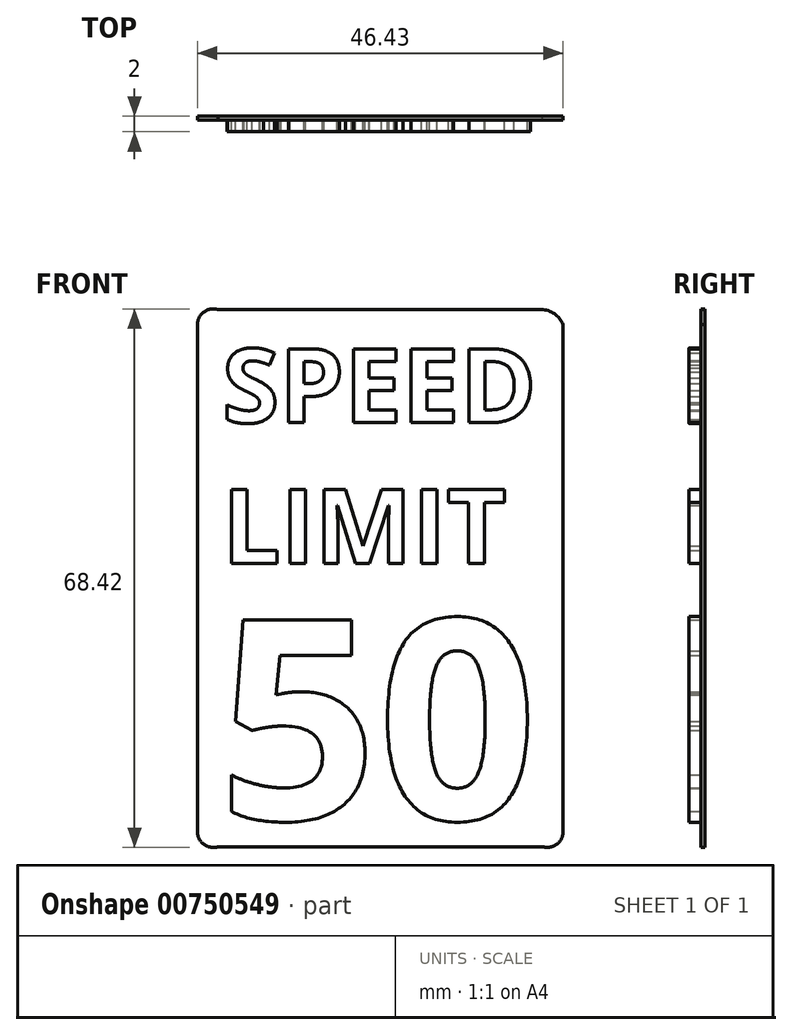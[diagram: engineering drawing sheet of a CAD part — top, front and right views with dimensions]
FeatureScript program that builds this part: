
annotation { "Feature Type Name" : "Feature", "Feature Type Description" : "" }
export const myFeature = defineFeature(function(context is Context, id is Id, definition is map)
    precondition{}
    {
        {
            var Q0;
            Q0=qCreatedBy(makeId("Front.planeOp"),FACE);
            var sketch = newSketch(context, id + "F0", { "sketchPlane" : qUnion([Q0])});
            skLineSegment(sketch, "E0", {"start": v(0, -30.25) * mm, "end": v(0, 34.16) * mm});
            skLineSegment(sketch, "E1", {"start": v(46.43, 34.16) * mm, "end": v(46.43, -30.25) * mm});
            skArc(sketch, "E2", {"start": v(43.8, -32.15) * mm, "mid": v(45.6, -31.87) * mm, "end": v(46.43, -30.25) * mm});
            skArc(sketch, "E3", {"start": v(0, -30.25) * mm, "mid": v(0.84, -31.88) * mm, "end": v(2.65, -32.15) * mm});
            skArc(sketch, "E4", {"start": v(2.62, 36.06) * mm, "mid": v(0.83, 35.78) * mm, "end": v(0, 34.16) * mm});
            skLineSegment(sketch, "E5", {"start": v(2.62, 36.06) * mm, "end": v(43.67, 36.06) * mm});
            skLineSegment(sketch, "E6", {"start": v(2.65, -32.15) * mm, "end": v(43.8, -32.15) * mm});
            skArc(sketch, "E7", {"start": v(46.43, 34.16) * mm, "mid": v(45.34, 35.54) * mm, "end": v(43.67, 36.06) * mm});
            skLineSegment(sketch, "E8.bottom", {"start": v(2, 34.16) * mm, "end": v(44.43, 34.16) * mm});
            skLineSegment(sketch, "E8.top", {"start": v(2, -30.25) * mm, "end": v(44.43, -30.25) * mm});
            skLineSegment(sketch, "E8.left", {"start": v(2, 34.16) * mm, "end": v(2, -30.25) * mm});
            skLineSegment(sketch, "E8.right", {"start": v(44.43, 34.16) * mm, "end": v(44.43, -30.25) * mm});
            skSolve(sketch);
        }
        {
            var Q0;
            Q0 = qSketchRegion(id + "F0", true);
            var Q1;
            Q1=makeQuery(id+"F0.imprint","IMPRINT",FACE,{"disambiguationData":[TD([[makeQuery(id+"F0.imprint","IMPRINT",EDGE,{"derivedFrom":sQuery(id+"F0.wireOp",EDGE,"E8.bottom")}),-1.0]])]});
            extrude(context, id + "F1", {"entities" : qUnion([Q0, Q1]), "depth" : 0.5 * mm, "offsetDistance" : 25 * mm});
        }
        {
            var Q0;
            Q0=qCreatedBy(makeId("Front.planeOp"),FACE);
            var sketch = newSketch(context, id + "F2", { "sketchPlane" : qUnion([Q0])});
            skText(sketch, "E9", { "text": "SPEED \nLIMIT\n", "fontName": "OpenSans-Bold.ttf"});
            skText(sketch, "E10", { "text": "50", "fontName": "OpenSans-Bold.ttf"});
            const initialGuessF2  = {"E9": [0.00312, 0.0217, 1, 0, 0.00946], "E10": [0.00257, -0.02871, 1, 0, 0.0256]};
            skSetInitialGuess(sketch, initialGuessF2);
            skSolve(sketch);
        }
        {
            var Q0;
            Q0 = qSketchRegion(id + "F2", true);
            extrude(context, id + "F3", {"entities" : qUnion([Q0]), "operationType" : NewBodyOperationType.ADD, "depth" : 2 * mm, "offsetDistance" : 25 * mm});
        }
    });
